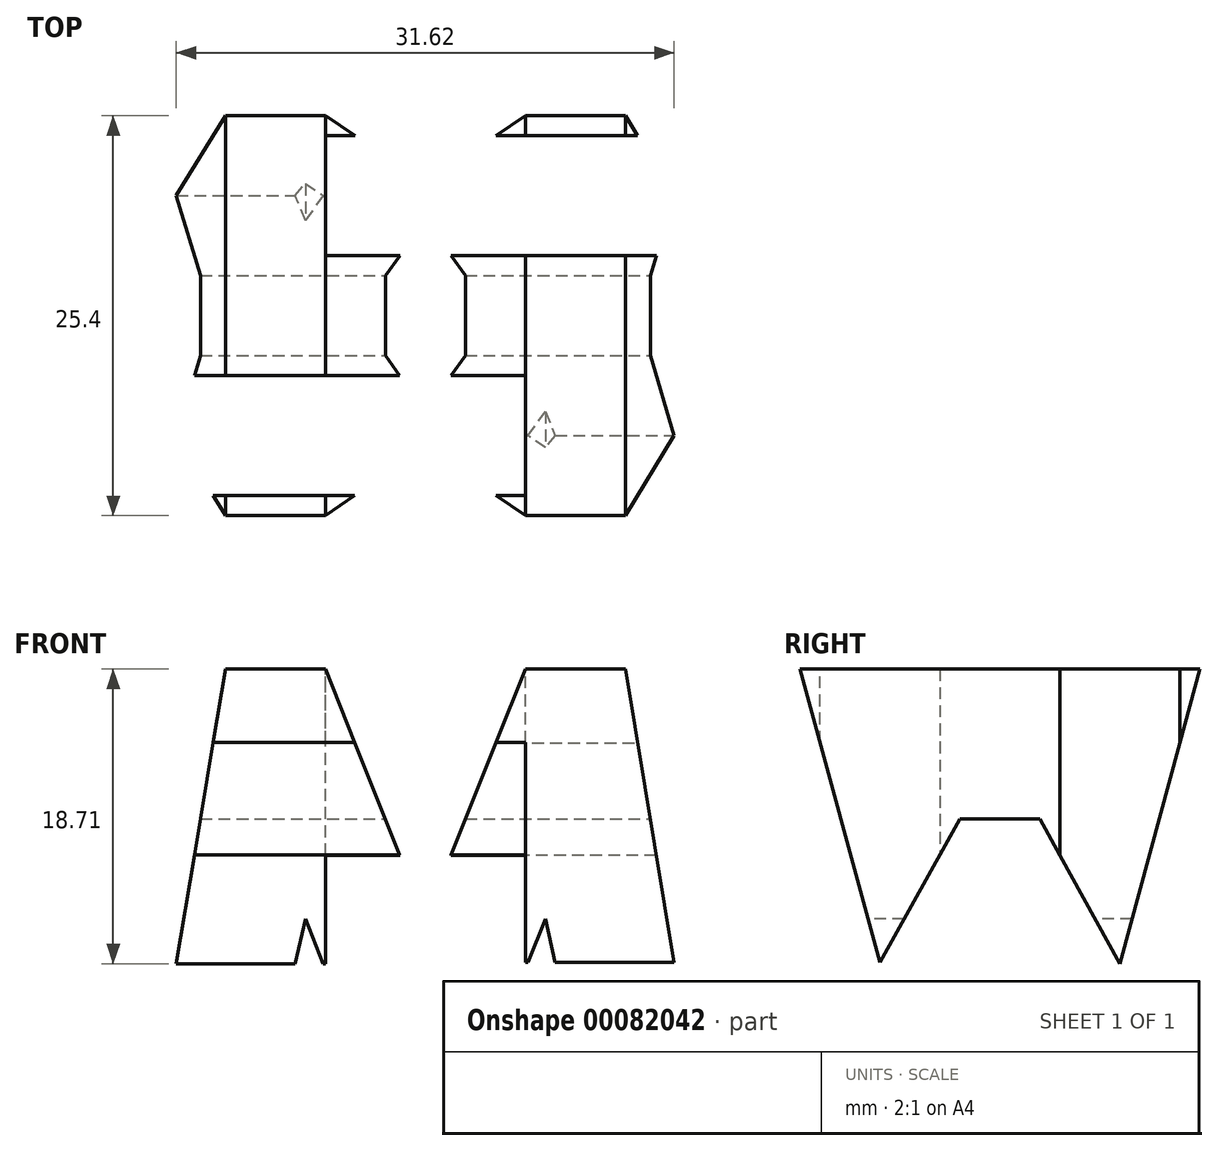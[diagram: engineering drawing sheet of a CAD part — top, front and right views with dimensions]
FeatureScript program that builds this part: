
annotation { "Feature Type Name" : "Feature", "Feature Type Description" : "" }
export const myFeature = defineFeature(function(context is Context, id is Id, definition is map)
    precondition{}
    {
        {
            var Q0;
            Q0=qCreatedBy(makeId("Front.planeOp"),FACE);
            var sketch = newSketch(context, id + "F0", { "sketchPlane" : qUnion([Q0])});
            skLineSegment(sketch, "E0", {"start": v(0, 0) * mm, "end": v(38.1, 0) * mm});
            skLineSegment(sketch, "E1", {"start": v(38.1, 0) * mm, "end": v(38.1, 38.1) * mm});
            skLineSegment(sketch, "E2", {"start": v(38.1, 38.1) * mm, "end": v(0, 38.1) * mm});
            skLineSegment(sketch, "E3", {"start": v(0, 0) * mm, "end": v(0, 38.1) * mm});
            skSolve(sketch);
        }
        {
            var Q0;
            Q0 = qSketchRegion(id + "F0", true);
            extrude(context, id + "F1", {"entities" : qUnion([Q0]), "depth" : 38.1 * mm});
        }
        {
            var Q0;
            Q0=qCreatedBy(makeId("Front.planeOp"),FACE);
            cPlane(context, id + "F2", {"entities" : qUnion([Q0]), "cplaneType" : CPlaneType.OFFSET, "offset" : 38.1 * mm, "width" : 152.4 * mm, "height" : 152.4 * mm});
        }
        {
            var Q0;
            Q0=qCreatedBy(makeId("Right.planeOp"),FACE);
            cPlane(context, id + "F3", {"entities" : qUnion([Q0]), "cplaneType" : CPlaneType.OFFSET, "offset" : 38.1 * mm, "width" : 152.4 * mm, "height" : 152.4 * mm});
        }
        {
            var Q0;
            Q0=qCreatedBy(makeId("Top.planeOp"),FACE);
            cPlane(context, id + "F4", {"entities" : qUnion([Q0]), "cplaneType" : CPlaneType.OFFSET, "offset" : 38.1 * mm, "width" : 152.4 * mm, "height" : 152.4 * mm});
        }
        {
            var Q0;
            Q0=qCreatedBy(id+"F3.planeOp",FACE);
            var sketch = newSketch(context, id + "F5", { "sketchPlane" : qUnion([Q0])});
            skLineSegment(sketch, "E4", {"start": v(-38.1, 0) * mm, "end": v(-38.1, 38.1) * mm});
            skLineSegment(sketch, "E5", {"start": v(-38.1, 38.1) * mm, "end": v(0, 38.1) * mm});
            skLineSegment(sketch, "E6", {"start": v(0, 38.1) * mm, "end": v(0, 0) * mm});
            skLineSegment(sketch, "E7", {"start": v(-31.75, 38.1) * mm, "end": v(-26.67, 19.47) * mm});
            skLineSegment(sketch, "E8", {"start": v(-26.67, 19.47) * mm, "end": v(-21.59, 28.58) * mm});
            skLineSegment(sketch, "E9", {"start": v(-21.59, 28.58) * mm, "end": v(-16.51, 28.58) * mm});
            skLineSegment(sketch, "E10", {"start": v(-16.51, 28.58) * mm, "end": v(-11.43, 19.39) * mm});
            skLineSegment(sketch, "E11", {"start": v(-11.43, 19.39) * mm, "end": v(-6.35, 38.1) * mm});
            skLineSegment(sketch, "E12", {"start": v(-38.1, 38.1) * mm, "end": v(-31.75, 38.1) * mm});
            skLineSegment(sketch, "E13", {"start": v(-6.35, 38.1) * mm, "end": v(0, 38.1) * mm});
            skLineSegment(sketch, "E14", {"start": v(-31.75, 38.1) * mm, "end": v(-38.1, 38.1) * mm});
            skPoint(sketch, "E15.end.orphan", {"position": v(-19.05, 0) * mm});
            skLineSegment(sketch, "E16", {"start": v(-38.1, 38.1) * mm, "end": v(-31.56, 0) * mm});
            skLineSegment(sketch, "E17", {"start": v(0, 38.1) * mm, "end": v(-6.16, 0) * mm});
            skLineSegment(sketch, "E18", {"start": v(-25.21, 0) * mm, "end": v(-18.86, 15.88) * mm});
            skLineSegment(sketch, "E19", {"start": v(-18.86, 15.88) * mm, "end": v(-12.51, 0) * mm});
            skLineSegment(sketch, "E20", {"start": v(-31.56, 0) * mm, "end": v(-25.21, 0) * mm});
            skLineSegment(sketch, "E21", {"start": v(-12.51, 0) * mm, "end": v(-6.16, 0) * mm});
            skLineSegment(sketch, "E22", {"start": v(-25.21, 0) * mm, "end": v(-12.51, 0) * mm});
            skLineSegment(sketch, "E23", {"start": v(-38.1, 0) * mm, "end": v(-31.56, 0) * mm});
            skLineSegment(sketch, "E24", {"start": v(-6.16, 0) * mm, "end": v(0, 0) * mm});
            skSolve(sketch);
        }
        {
            var Q0;
            Q0=makeQuery(id+"F5.imprint","IMPRINT",FACE,{"disambiguationData":[TD([[makeQuery(id+"F5.imprint","IMPRINT",EDGE,{"derivedFrom":sQuery(id+"F5.wireOp",EDGE,"E5")}),-1.0]])]});
            var Q1;
            Q1=makeQuery(id+"F5.imprint","IMPRINT",FACE,{"disambiguationData":[TD([[makeQuery(id+"F5.imprint","IMPRINT",EDGE,{"derivedFrom":sQuery(id+"F5.wireOp",EDGE,"E4")}),-1.0]])]});
            var Q2;
            Q2=makeQuery(id+"F5.imprint","IMPRINT",FACE,{"disambiguationData":[TD([[makeQuery(id+"F5.imprint","IMPRINT",EDGE,{"derivedFrom":sQuery(id+"F5.wireOp",EDGE,"E18")}),-1.0]])]});
            var Q3;
            Q3=makeQuery(id+"F5.imprint","IMPRINT",FACE,{"disambiguationData":[TD([[makeQuery(id+"F5.imprint","IMPRINT",EDGE,{"derivedFrom":sQuery(id+"F5.wireOp",EDGE,"E6")}),-1.0]])]});
            extrude(context, id + "F6", {"entities" : qUnion([Q0, Q1, Q2, Q3]), "operationType" : NewBodyOperationType.REMOVE, "oppositeDirection" : true, "depth" : 38.1 * mm});
        }
        {
            var Q0;
            Q0=qCreatedBy(id+"F2.planeOp",FACE);
            var sketch = newSketch(context, id + "F7", { "sketchPlane" : qUnion([Q0])});
            skLineSegment(sketch, "E25", {"start": v(0, 0) * mm, "end": v(38.1, 0) * mm});
            skLineSegment(sketch, "E26", {"start": v(38.1, 0) * mm, "end": v(38.1, 38.1) * mm});
            skLineSegment(sketch, "E27", {"start": v(38.1, 38.1) * mm, "end": v(0, 38.1) * mm});
            skLineSegment(sketch, "E28", {"start": v(0, 38.1) * mm, "end": v(0, 0) * mm});
            skLineSegment(sketch, "E29", {"start": v(0, 0) * mm, "end": v(6.35, 38.1) * mm});
            skLineSegment(sketch, "E30", {"start": v(6.35, 38.1) * mm, "end": v(12.7, 38.1) * mm});
            skLineSegment(sketch, "E31", {"start": v(12.7, 38.1) * mm, "end": v(19.05, 22.23) * mm});
            skLineSegment(sketch, "E32", {"start": v(19.05, 22.23) * mm, "end": v(25.4, 38.1) * mm});
            skLineSegment(sketch, "E33", {"start": v(25.4, 38.1) * mm, "end": v(31.75, 38.1) * mm});
            skLineSegment(sketch, "E34", {"start": v(31.75, 38.1) * mm, "end": v(38.1, 0) * mm});
            skLineSegment(sketch, "E35", {"start": v(31.75, 0) * mm, "end": v(26.67, 22.23) * mm});
            skLineSegment(sketch, "E36", {"start": v(26.67, 22.22) * mm, "end": v(21.6, 9.53) * mm});
            skLineSegment(sketch, "E37", {"start": v(21.6, 9.53) * mm, "end": v(16.51, 9.53) * mm});
            skLineSegment(sketch, "E38", {"start": v(16.51, 9.53) * mm, "end": v(11.43, 22.23) * mm});
            skLineSegment(sketch, "E39", {"start": v(11.43, 22.23) * mm, "end": v(6.35, 0) * mm});
            skLineSegment(sketch, "E40", {"start": v(0, 38.1) * mm, "end": v(6.35, 38.1) * mm});
            skLineSegment(sketch, "E41", {"start": v(12.7, 38.1) * mm, "end": v(25.4, 38.1) * mm});
            skLineSegment(sketch, "E42", {"start": v(31.75, 38.1) * mm, "end": v(38.1, 38.1) * mm});
            skSolve(sketch);
        }
        {
            var Q0;
            Q0=makeQuery(id+"F7.imprint","IMPRINT",FACE,{"disambiguationData":[TD([[makeQuery(id+"F7.imprint","IMPRINT",EDGE,{"derivedFrom":sQuery(id+"F7.wireOp",EDGE,"E31")}),1.0]])]});
            var Q1;
            {var subQ0=sQuery(id+"F7.wireOp",EDGE,"E35");Q1=makeQuery(id+"F7.imprint","IMPRINT",FACE,{"disambiguationData":[TD([[makeQuery(id+"F7.imprint","IMPRINT",EDGE,{"derivedFrom":subQ0}),1.0]])]});}
            var Q2;
            Q2=makeQuery(id+"F7.imprint","IMPRINT",FACE,{"disambiguationData":[TD([[makeQuery(id+"F7.imprint","IMPRINT",EDGE,{"derivedFrom":sQuery(id+"F7.wireOp",EDGE,"E28")}),1.0]])]});
            var Q3;
            Q3=makeQuery(id+"F7.imprint","IMPRINT",FACE,{"disambiguationData":[TD([[makeQuery(id+"F7.imprint","IMPRINT",EDGE,{"derivedFrom":sQuery(id+"F7.wireOp",EDGE,"E26")}),1.0]])]});
            extrude(context, id + "F8", {"entities" : qUnion([Q0, Q1, Q2, Q3]), "operationType" : NewBodyOperationType.REMOVE, "oppositeDirection" : true, "depth" : 38.1 * mm});
        }
        {
            var Q0;
            Q0=qCreatedBy(id+"F4.planeOp",FACE);
            var sketch = newSketch(context, id + "F9", { "sketchPlane" : qUnion([Q0])});
            skLineSegment(sketch, "E43", {"start": v(0, 0) * mm, "end": v(0, -38.1) * mm});
            skLineSegment(sketch, "E44", {"start": v(0, -38.1) * mm, "end": v(38.1, -38.1) * mm});
            skLineSegment(sketch, "E45", {"start": v(38.1, -38.1) * mm, "end": v(38.1, 0) * mm});
            skLineSegment(sketch, "E46", {"start": v(38.1, 0) * mm, "end": v(0, 0) * mm});
            skLineSegment(sketch, "E47", {"start": v(38.1, -7.62) * mm, "end": v(12.7, -7.62) * mm});
            skLineSegment(sketch, "E48", {"start": v(12.7, -7.62) * mm, "end": v(12.7, -15.24) * mm});
            skLineSegment(sketch, "E49", {"start": v(12.7, -15.24) * mm, "end": v(38.1, -15.24) * mm});
            skLineSegment(sketch, "E50", {"start": v(0, -22.86) * mm, "end": v(25.4, -22.86) * mm});
            skLineSegment(sketch, "E51", {"start": v(25.4, -22.86) * mm, "end": v(25.4, -30.48) * mm});
            skLineSegment(sketch, "E52", {"start": v(25.4, -30.48) * mm, "end": v(0, -30.48) * mm});
            skSolve(sketch);
        }
        {
            var Q0;
            {var subQ0=sQuery(id+"F9.wireOp",EDGE,"E47");Q0=makeQuery(id+"F9.imprint","IMPRINT",FACE,{"disambiguationData":[TD([[makeQuery(id+"F9.imprint","IMPRINT",EDGE,{"derivedFrom":subQ0}),1.0]])]});}
            var Q1;
            {var subQ0=sQuery(id+"F9.wireOp",EDGE,"E50");Q1=makeQuery(id+"F9.imprint","IMPRINT",FACE,{"disambiguationData":[TD([[makeQuery(id+"F9.imprint","IMPRINT",EDGE,{"derivedFrom":subQ0}),-1.0]])]});}
            extrude(context, id + "F10", {"entities" : qUnion([Q0, Q1]), "operationType" : NewBodyOperationType.REMOVE, "oppositeDirection" : true, "depth" : 38.1 * mm});
        }
    });
